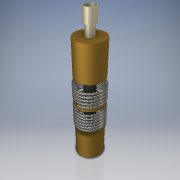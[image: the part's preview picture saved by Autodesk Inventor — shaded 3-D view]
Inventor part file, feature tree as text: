
AUTODESK INVENTOR PART (.ipt)
format: ipt  version: 2018 (Build 220112000, 112)  size: 352,768 bytes
history: native  units: in
note: dims shown in document units (in); Inventor stores cm internally (conversion verified against a paired STEP export)
features: sketch x9, extrude x6, helix x2, revolve x1
ambient origin geometry x8: Origin, YZ Plane, XZ Plane, XY Plane, X Axis, Y Axis, Z Axis, Center Point
bodies: Body1 (feature_tree)
feature tree (18):
  extrude  "Extrusion3"  Depth=0.5in
  extrude  "Extrusion4"  Depth=0.3in
  extrude  "Extrusion5"  Depth=0.03in
  extrude  "Extrusion6"  Depth=1.25in
  extrude  "Extrusion7"  Depth=0.5in
  helix  "Coil1"  [1 undecoded]
  extrude  "Extrusion8"  Depth=0.625in
  helix  "Coil2"  [1 undecoded]
  revolve  "Revolution1"  [1 undecoded]
  sketch  "Sketch3"  dims[d6=0.44in d7=0.5in]
  sketch  "Sketch4"  dims[d8=0.44in d9=0.0in d10=0.3in]
  sketch  "Sketch5"  dims[d11=0.1in d12=0.0in d13=0.03in]
  sketch  "Sketch6"  dims[d14=0.44in d15=0.0in d16=1.25in]
  sketch  "Sketch7"  dims[d17=1.5in d18=0.0in d19=0.5in d20=2.5in d21=0.0in]
  sketch  "Sketch8"  dims[d23=0.1in]
  sketch  "Sketch9"  dims[d24=0.15in d25=1.0in d26=4.7244in d27=0.0in d28=90.0deg d29=90.0deg d30=0.0in d31=0.0in d32=0.625in d33=1.25in]
  sketch  "Sketch11"  dims[d37=0.0in d38=0.0in d39=90.0deg d40=90.0deg d41=0.0in d42=4.7244in d43=0.75in d44=0.15in d45=0.625in d47=0.1in d48=0.25in d49=0.1in d50=0.65in d51=90.0deg d52=3.1in]
  sketch  "Sketch10"  dims[d34=1.25in d35=1.25in d36=0.0in]
note: 3 required parameter values undecoded (feature->parameter linkage not recoverable at this tier; creation-order binding heuristic only, values carry confidence <= 0.55)